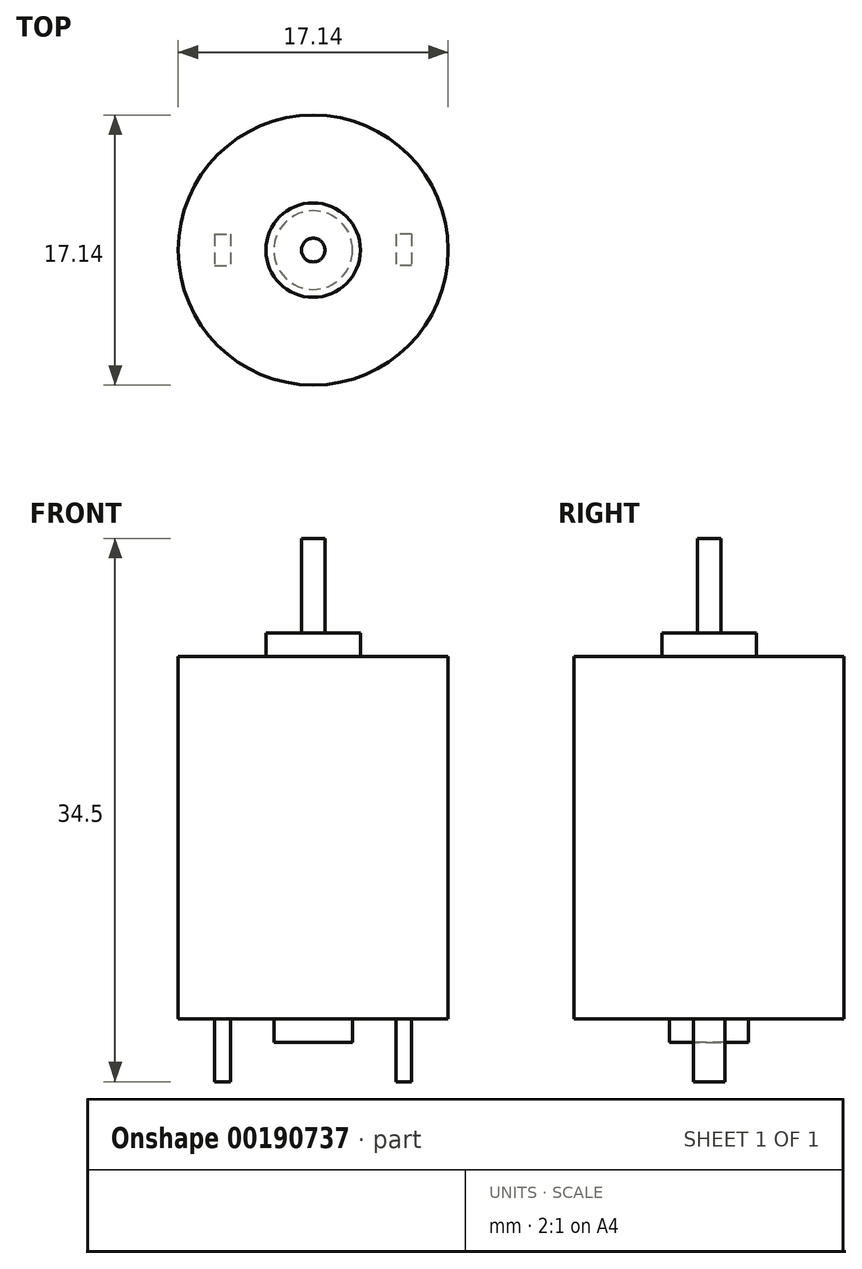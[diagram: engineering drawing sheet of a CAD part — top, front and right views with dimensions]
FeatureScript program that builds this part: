
annotation { "Feature Type Name" : "Feature", "Feature Type Description" : "" }
export const myFeature = defineFeature(function(context is Context, id is Id, definition is map)
    precondition{}
    {
        {
            var Q0;
            Q0=qCreatedBy(makeId("Front.planeOp"),FACE);
            var sketch = newSketch(context, id + "F0", { "sketchPlane" : qUnion([Q0])});
            skLineSegment(sketch, "E0.bottom", {"start": v(2.5, 0) * mm, "end": v(8.57, 0) * mm});
            skLineSegment(sketch, "E0.top", {"start": v(3, 23) * mm, "end": v(8.57, 23) * mm});
            skLineSegment(sketch, "E0.left", {"start": v(0, 0) * mm, "end": v(0, 24.5) * mm, "construction": true});
            skLineSegment(sketch, "E0.right", {"start": v(8.57, 0) * mm, "end": v(8.57, 23) * mm});
            skLineSegment(sketch, "E1", {"start": v(3, 23) * mm, "end": v(3, 24.5) * mm});
            skLineSegment(sketch, "E2", {"start": v(3, 24.5) * mm, "end": v(0, 24.5) * mm});
            skLineSegment(sketch, "E3", {"start": v(2.5, 0) * mm, "end": v(2.5, -1.5) * mm});
            skLineSegment(sketch, "E4", {"start": v(2.5, -1.5) * mm, "end": v(0, -1.5) * mm});
            skLineSegment(sketch, "E5", {"start": v(0, -1.5) * mm, "end": v(0, 0) * mm, "construction": true});
            skLineSegment(sketch, "E6", {"start": v(0, -1.5) * mm, "end": v(0, 24.5) * mm});
            skSolve(sketch);
        }
        {
            var Q0;
            Q0 = qSketchRegion(id + "F0", true);
            var Q1;
            Q1=sQuery(id+"F0.wireOp",EDGE,"E6");
            revolve(context, id + "F1", {"entities" : qUnion([Q0]), "axis" : qUnion([Q1]), "revolveType" : RevolveType.FULL});
        }
        {
            var Q0;
            Q0=makeQuery(id+"F1.opRevolve","SWEPT_FACE",FACE,{"disambiguationData":[OSD([sQuery(id+"F0.wireOp",EDGE,"E2")])]});
            var sketch = newSketch(context, id + "F2", { "sketchPlane" : qUnion([Q0])});
            skCircle(sketch, "E7", {"center": v(0, 0) * mm, "radius": 0.75 * mm});
            skSolve(sketch);
        }
        {
            var Q0;
            Q0=makeQuery(id+"F2.imprint","IMPRINT",FACE,{"disambiguationData":[TD([[makeQuery(id+"F2.imprint","IMPRINT",EDGE,{"derivedFrom":sQuery(id+"F2.wireOp",EDGE,"E7")}),1.0]])]});
            extrude(context, id + "F3", {"entities" : qUnion([Q0]), "operationType" : NewBodyOperationType.ADD, "depth" : 6 * mm});
        }
        {
            var Q0;
            Q0=makeQuery(id+"F1.opRevolve","SWEPT_FACE",FACE,{"disambiguationData":[OSD([sQuery(id+"F0.wireOp",EDGE,"E0.bottom")])]});
            var sketch = newSketch(context, id + "F4", { "sketchPlane" : qUnion([Q0])});
            skLineSegment(sketch, "E8", {"start": v(0, 0) * mm, "end": v(8.57, 0) * mm, "construction": true});
            skLineSegment(sketch, "E9", {"start": v(0, 0) * mm, "end": v(0, 8.57) * mm, "construction": true});
            skLineSegment(sketch, "E10.bottom", {"start": v(6.25, -1) * mm, "end": v(5.25, -1) * mm});
            skLineSegment(sketch, "E10.top", {"start": v(6.25, 1) * mm, "end": v(5.25, 1) * mm});
            skLineSegment(sketch, "E10.left", {"start": v(6.25, -1) * mm, "end": v(6.25, 1) * mm});
            skLineSegment(sketch, "E10.right", {"start": v(5.25, -1) * mm, "end": v(5.25, 1) * mm});
            skPoint(sketch, "E10.middle", {"position": v(5.75, 0) * mm});
            skPoint(sketch, "E11.MirrorP", {"position": v(-5.75, 0) * mm});
            skLineSegment(sketch, "E12.MirrorCS", {"start": v(-6.25, -1) * mm, "end": v(-5.25, -1) * mm});
            skLineSegment(sketch, "E13.MirrorCS", {"start": v(-6.25, 1) * mm, "end": v(-5.25, 1) * mm});
            skLineSegment(sketch, "E14.MirrorCS", {"start": v(-6.25, -1) * mm, "end": v(-6.25, 1) * mm});
            skLineSegment(sketch, "E15.MirrorCS", {"start": v(-5.25, -1) * mm, "end": v(-5.25, 1) * mm});
            skSolve(sketch);
        }
        {
            var Q0;
            Q0 = qSketchRegion(id + "F4", true);
            extrude(context, id + "F5", {"entities" : qUnion([Q0]), "operationType" : NewBodyOperationType.ADD, "depth" : 4 * mm});
        }
    });
